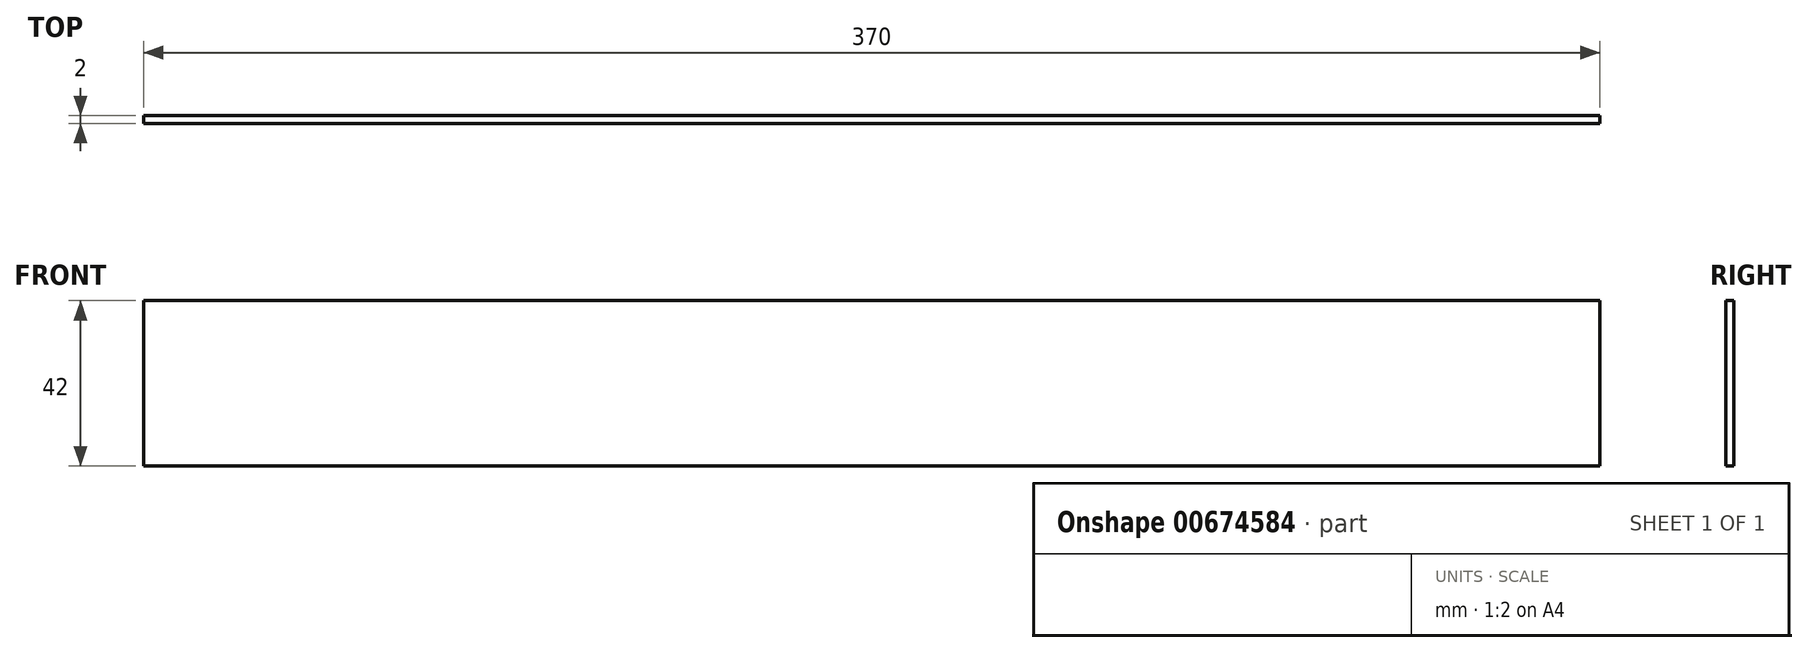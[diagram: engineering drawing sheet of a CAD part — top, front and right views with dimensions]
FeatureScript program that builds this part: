
annotation { "Feature Type Name" : "Feature", "Feature Type Description" : "" }
export const myFeature = defineFeature(function(context is Context, id is Id, definition is map)
    precondition{}
    {
        {
            var Q0;
            Q0=qCreatedBy(makeId("Front.planeOp"),FACE);
            var sketch = newSketch(context, id + "F0", { "sketchPlane" : qUnion([Q0])});
            skLineSegment(sketch, "E0.bottom", {"start": v(185, 21) * mm, "end": v(-185, 21) * mm});
            skLineSegment(sketch, "E0.top", {"start": v(185, -21) * mm, "end": v(-185, -21) * mm});
            skLineSegment(sketch, "E0.left", {"start": v(185, 21) * mm, "end": v(185, -21) * mm});
            skLineSegment(sketch, "E0.right", {"start": v(-185, 21) * mm, "end": v(-185, -21) * mm});
            skPoint(sketch, "E0.middle", {"position": v(0, 0) * mm});
            skSolve(sketch);
        }
        {
            var Q0;
            Q0 = qSketchRegion(id + "F0", true);
            extrude(context, id + "F1", {"entities" : qUnion([Q0]), "depth" : 2 * mm, "offsetDistance" : 25 * mm});
        }
    });
